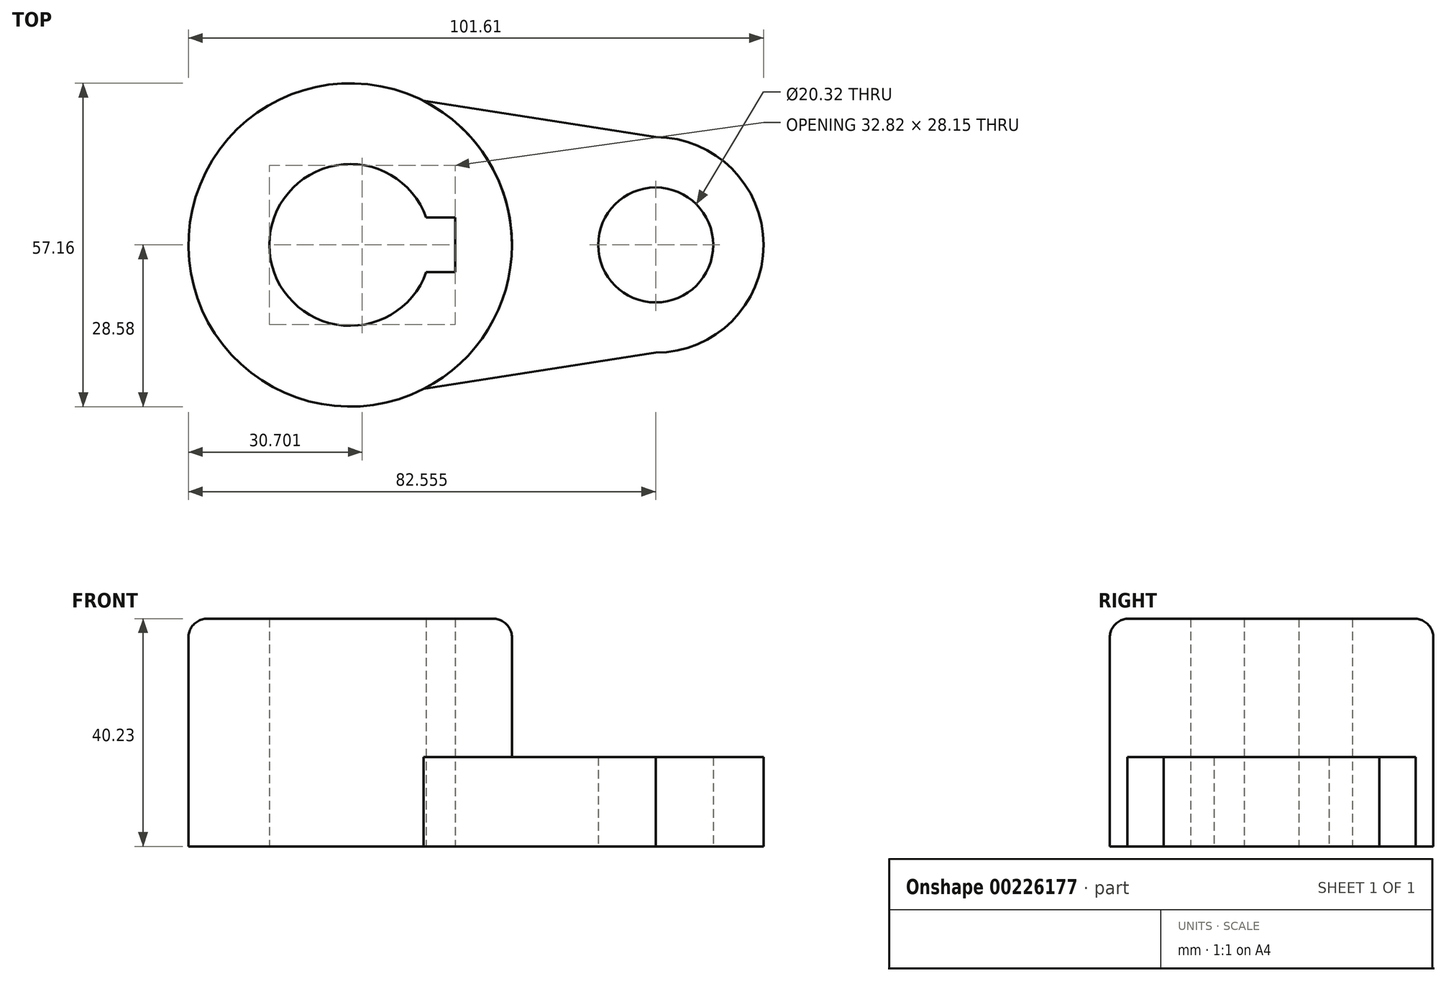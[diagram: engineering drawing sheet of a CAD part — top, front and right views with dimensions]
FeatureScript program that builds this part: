
annotation { "Feature Type Name" : "Feature", "Feature Type Description" : "" }
export const myFeature = defineFeature(function(context is Context, id is Id, definition is map)
    precondition{}
    {
        {
            var Q0;
            Q0=qCreatedBy(makeId("Top.planeOp"),FACE);
            var sketch = newSketch(context, id + "F0", { "sketchPlane" : qUnion([Q0])});
            skCircle(sketch, "E0", {"center": v(0, 0) * mm, "radius": 28.57 * mm});
            skArc(sketch, "E1", {"start": v(13.45, 4.83) * mm, "mid": v(-14.29, 0) * mm, "end": v(13.45, -4.83) * mm});
            skCircle(sketch, "E2", {"center": v(53.98, 0) * mm, "radius": 10.16 * mm});
            skLineSegment(sketch, "E3.bottom", {"start": v(18.53, -4.83) * mm, "end": v(13.45, -4.83) * mm});
            skLineSegment(sketch, "E3.top", {"start": v(18.53, 4.83) * mm, "end": v(13.45, 4.83) * mm});
            skLineSegment(sketch, "E3.left", {"start": v(18.53, -4.83) * mm, "end": v(18.53, 4.83) * mm});
            skPoint(sketch, "E3.middle", {"position": v(9.75, 0) * mm});
            skPoint(sketch, "E3.right.end.orphan", {"position": v(0.98, 4.83) * mm});
            skPoint(sketch, "E4.orphan", {"position": v(0.98, -4.83) * mm});
            skArc(sketch, "E5", {"start": v(53.98, 19.05) * mm, "mid": v(73.03, 0) * mm, "end": v(53.98, -19.05) * mm});
            skLineSegment(sketch, "E6", {"start": v(53.98, 19.05) * mm, "end": v(12.96, 25.47) * mm});
            skLineSegment(sketch, "E7", {"start": v(12.96, -25.47) * mm, "end": v(53.98, -19.05) * mm});
            skSolve(sketch);
        }
        {
            var Q0;
            Q0=makeQuery(id+"F0.imprint","IMPRINT",FACE,{"disambiguationData":[TD([[makeQuery(id+"F0.imprint","IMPRINT",EDGE,{"derivedFrom":sQuery(id+"F0.wireOp",EDGE,"E1")}),-1.0]])]});
            extrude(context, id + "F1", {"entities" : qUnion([Q0]), "depth" : 40.23 * mm});
        }
        {
            var Q0;
            Q0=makeQuery(id+"F0.imprint","IMPRINT",FACE,{"disambiguationData":[TD([[makeQuery(id+"F0.imprint","IMPRINT",EDGE,{"derivedFrom":sQuery(id+"F0.wireOp",EDGE,"E2")}),-1.0]])]});
            extrude(context, id + "F2", {"entities" : qUnion([Q0]), "operationType" : NewBodyOperationType.ADD, "depth" : 15.77 * mm});
        }
        {
            var Q0;
            Q0=makeQuery(id+"F1.opExtrude","CAP_EDGE",EDGE,{"disambiguationData":[OSD([sQuery(id+"F0.wireOp",EDGE,"E0")])],"isStart":false});
            fillet(context, id + "F3", {"entities" : qUnion([Q0]), "radius" : 3.3 * mm, "tangentPropagation" : true, "allowEdgeOverflow" : false});
        }
    });
